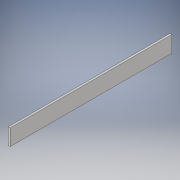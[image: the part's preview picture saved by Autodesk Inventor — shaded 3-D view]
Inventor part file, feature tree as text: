
AUTODESK INVENTOR PART (.ipt)
format: ipt  version: 2018 (Build 220112000, 112)  size: 92,160 bytes
history: native  units: in
note: dims shown in document units (in); Inventor stores cm internally (conversion verified against a paired STEP export)
features: extrude x1, sketch x1
ambient origin geometry x8: Origin, YZ Plane, XZ Plane, XY Plane, X Axis, Y Axis, Z Axis, Center Point
bodies: Solid1 (feature_tree)
feature tree (2):
  extrude  "Extrusion1"  Depth=10.0in
  sketch  "Sketch1"  dims[d0=1.0in d1=10.0in d2=0.125in d3=0.0in]
